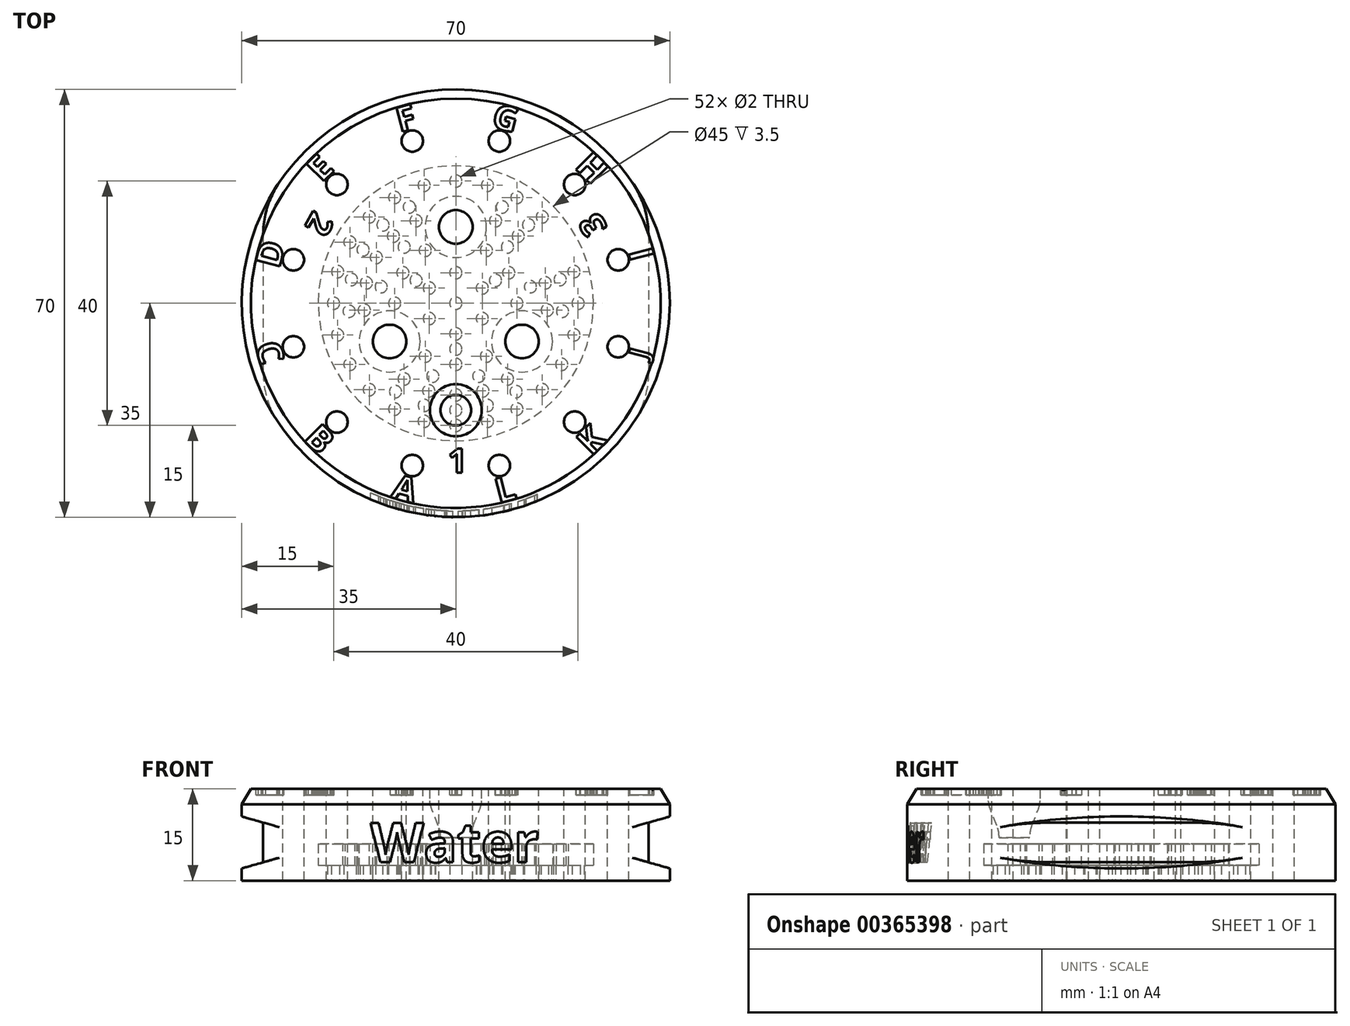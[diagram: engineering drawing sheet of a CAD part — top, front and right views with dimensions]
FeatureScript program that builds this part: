
annotation { "Feature Type Name" : "Feature", "Feature Type Description" : "" }
export const myFeature = defineFeature(function(context is Context, id is Id, definition is map)
    precondition{}
    {
        {
            var Q0;
            Q0=qCreatedBy(makeId("Top.planeOp"),FACE);
            var sketch = newSketch(context, id + "F0", { "sketchPlane" : qUnion([Q0])});
            skCircle(sketch, "E0", {"center": v(0, 0) * mm, "radius": 35 * mm});
            skSolve(sketch);
        }
        {
            var Q0;
            Q0=qSketchRegion(id+"F0",true);
            extrude(context, id + "F1", {"entities" : qUnion([Q0]), "depth" : 15 * mm});
        }
        {
            var Q0;
            Q0=qCreatedBy(makeId("Front.planeOp"),FACE);
            var sketch = newSketch(context, id + "F2", { "sketchPlane" : qUnion([Q0])});
            skText(sketch, "E1", { "text": "Water", "fontName": "OpenSans-Bold.ttf"});
            const initialGuessF2  = {"E1": [-0.01396, 0.003, 1, 0, 0.0065]};
            skSetInitialGuess(sketch, initialGuessF2);
            skSolve(sketch);
        }
        {
            var Q0;
            Q0=qSketchRegion(id+"F2",true);
            var Q1;
            Q1=makeQuery(id+"F1.opExtrude","SWEPT_FACE",FACE,{"disambiguationData":[OSD([sQuery(id+"F0.wireOp",EDGE,"E0")])]});
            extrude(context, id + "F3", {"entities" : qUnion([Q0]), "operationType" : NewBodyOperationType.REMOVE, "endBound" : BoundingType.THROUGH_ALL, "endBoundEntityFace" : qUnion([Q1]), "depth" : 25 * mm});
        }
        {
            var Q0;
            Q0=makeQuery(id+"F1.opExtrude","CAP_FACE",FACE,{"disambiguationData":[OSD([sQuery(id+"F0.wireOp",EDGE,"E0")])],"isStart":false});
            var sketch = newSketch(context, id + "F4", { "sketchPlane" : qUnion([Q0])});
            skCircle(sketch, "E2", {"center": v(0, 0) * mm, "radius": 34 * mm});
            skSolve(sketch);
        }
        {
            var Q0;
            Q0=qSketchRegion(id+"F4",true);
            var Q1;
            Q1=makeQuery(id+"F1.opExtrude","CAP_FACE",FACE,{"disambiguationData":[OSD([sQuery(id+"F0.wireOp",EDGE,"E0")])],"isStart":true});
            extrude(context, id + "F5", {"entities" : qUnion([Q0]), "operationType" : NewBodyOperationType.ADD, "endBound" : BoundingType.UP_TO_SURFACE, "oppositeDirection" : true, "endBoundEntityFace" : qUnion([Q1]), "depth" : 25 * mm});
        }
        {
            var Q0;
            Q0=qCreatedBy(makeId("Front.planeOp"),FACE);
            var sketch = newSketch(context, id + "F6", { "sketchPlane" : qUnion([Q0])});
            skLineSegment(sketch, "E3", {"start": v(-35, 10.5) * mm, "end": v(-35, 2) * mm});
            skLineSegment(sketch, "E4", {"start": v(-35, 2) * mm, "end": v(-31.5, 3) * mm});
            skLineSegment(sketch, "E5", {"start": v(-31.5, 3) * mm, "end": v(-31.5, 9.5) * mm});
            skLineSegment(sketch, "E6", {"start": v(-31.5, 9.5) * mm, "end": v(-35, 10.5) * mm});
            skLineSegment(sketch, "E7.MirrorCS", {"start": v(35, 10.5) * mm, "end": v(35, 2) * mm});
            skLineSegment(sketch, "E8.MirrorCS", {"start": v(31.5, 9.5) * mm, "end": v(35, 10.5) * mm});
            skLineSegment(sketch, "E9.MirrorCS", {"start": v(35, 2) * mm, "end": v(31.5, 3) * mm});
            skLineSegment(sketch, "E10.MirrorCS", {"start": v(31.5, 3) * mm, "end": v(31.5, 9.5) * mm});
            skSolve(sketch);
        }
        {
            var Q0;
            Q0=qSketchRegion(id+"F6",true);
            extrude(context, id + "F7", {"entities" : qUnion([Q0]), "operationType" : NewBodyOperationType.REMOVE, "endBound" : BoundingType.THROUGH_ALL, "oppositeDirection" : true, "depth" : 25 * mm, "hasSecondDirection" : true, "secondDirectionBound" : BoundingType.THROUGH_ALL, "secondDirectionOppositeDirection" : false, "secondDirectionDepth" : 25 * mm});
        }
        {
            var Q0;
            {var subQ0=sQuery(id+"F0.wireOp",EDGE,"E0");Q0=makeQuery(id+"F7.boolean.opBoolean","INTERSECT",EDGE,{"disambiguationData":[OD(0.0)],"derivedFrom":[makeQuery(id+"F3.boolean.opBoolean","SPLIT",FACE,{"disambiguationData":[TD([makeQuery(id+"F1.opExtrude","CAP_FACE",FACE,{"disambiguationData":[OSD([subQ0])],"isStart":true})])],"derivedFrom":makeQuery(id+"F1.opExtrude","SWEPT_FACE",FACE,{"disambiguationData":[OSD([subQ0])]})}),makeQuery(id+"F7.opExtrude","SWEPT_FACE",FACE,{"disambiguationData":[OSD([sQuery(id+"F6.wireOp",EDGE,"E5")])]})]});}
            var Q1;
            {var subQ0=sQuery(id+"F0.wireOp",EDGE,"E0");Q1=makeQuery(id+"F7.boolean.opBoolean","INTERSECT",EDGE,{"disambiguationData":[OD(0.0)],"derivedFrom":[makeQuery(id+"F3.boolean.opBoolean","SPLIT",FACE,{"disambiguationData":[TD([makeQuery(id+"F1.opExtrude","CAP_FACE",FACE,{"disambiguationData":[OSD([subQ0])],"isStart":true})])],"derivedFrom":makeQuery(id+"F1.opExtrude","SWEPT_FACE",FACE,{"disambiguationData":[OSD([subQ0])]})}),makeQuery(id+"F7.opExtrude","SWEPT_FACE",FACE,{"disambiguationData":[OSD([sQuery(id+"F6.wireOp",EDGE,"E10.MirrorCS")])]})]});}
            var Q2;
            {var subQ0=sQuery(id+"F0.wireOp",EDGE,"E0");Q2=makeQuery(id+"F7.boolean.opBoolean","INTERSECT",EDGE,{"disambiguationData":[OD(1.0)],"derivedFrom":[makeQuery(id+"F3.boolean.opBoolean","SPLIT",FACE,{"disambiguationData":[TD([makeQuery(id+"F1.opExtrude","CAP_FACE",FACE,{"disambiguationData":[OSD([subQ0])],"isStart":true})])],"derivedFrom":makeQuery(id+"F1.opExtrude","SWEPT_FACE",FACE,{"disambiguationData":[OSD([subQ0])]})}),makeQuery(id+"F7.opExtrude","SWEPT_FACE",FACE,{"disambiguationData":[OSD([sQuery(id+"F6.wireOp",EDGE,"E10.MirrorCS")])]})]});}
            var Q3;
            {var subQ0=sQuery(id+"F0.wireOp",EDGE,"E0");Q3=makeQuery(id+"F7.boolean.opBoolean","INTERSECT",EDGE,{"disambiguationData":[OD(1.0)],"derivedFrom":[makeQuery(id+"F3.boolean.opBoolean","SPLIT",FACE,{"disambiguationData":[TD([makeQuery(id+"F1.opExtrude","CAP_FACE",FACE,{"disambiguationData":[OSD([subQ0])],"isStart":true})])],"derivedFrom":makeQuery(id+"F1.opExtrude","SWEPT_FACE",FACE,{"disambiguationData":[OSD([subQ0])]})}),makeQuery(id+"F7.opExtrude","SWEPT_FACE",FACE,{"disambiguationData":[OSD([sQuery(id+"F6.wireOp",EDGE,"E5")])]})]});}
            fillet(context, id + "F8", {"entities" : qUnion([Q0, Q1, Q2, Q3]), "radius" : 15 * mm, "tangentPropagation" : true, "allowEdgeOverflow" : false});
        }
        {
            var Q0;
            Q0=makeQuery(id+"F1.opExtrude","CAP_FACE",FACE,{"disambiguationData":[OSD([sQuery(id+"F0.wireOp",EDGE,"E0")])],"isStart":false});
            var sketch = newSketch(context, id + "F9", { "sketchPlane" : qUnion([Q0])});
            skCircle(sketch, "E11", {"center": v(0, 12.5) * mm, "radius": 2.75 * mm});
            skCircle(sketch, "E12.1.0", {"center": v(-10.83, -6.25) * mm, "radius": 2.75 * mm});
            skCircle(sketch, "E12.2.0", {"center": v(10.83, -6.25) * mm, "radius": 2.75 * mm});
            skPoint(sketch, "E12.center", {"position": v(0, 0) * mm});
            skCircle(sketch, "E13", {"center": v(0, 0) * mm, "radius": 12.5 * mm, "construction": true});
            skSolve(sketch);
        }
        {
            var Q0;
            Q0=qSketchRegion(id+"F9",true);
            extrude(context, id + "F10", {"entities" : qUnion([Q0]), "operationType" : NewBodyOperationType.REMOVE, "endBound" : BoundingType.THROUGH_ALL, "oppositeDirection" : true, "depth" : 25 * mm});
        }
        {
            var Q0;
            Q0=makeQuery(id+"F1.opExtrude","CAP_FACE",FACE,{"disambiguationData":[OSD([sQuery(id+"F0.wireOp",EDGE,"E0")])],"isStart":false});
            var sketch = newSketch(context, id + "F11", { "sketchPlane" : qUnion([Q0])});
            skCircle(sketch, "E14", {"center": v(0, -17.5) * mm, "radius": 2.5 * mm});
            skCircle(sketch, "E15", {"center": v(0, 0) * mm, "radius": 17.5 * mm, "construction": true});
            skSolve(sketch);
        }
        {
            var Q0;
            Q0=qSketchRegion(id+"F11",true);
            extrude(context, id + "F12", {"entities" : qUnion([Q0]), "operationType" : NewBodyOperationType.REMOVE, "endBound" : BoundingType.THROUGH_ALL, "oppositeDirection" : true, "depth" : 25 * mm});
        }
        {
            var Q0;
            Q0=makeQuery(id+"F1.opExtrude","CAP_FACE",FACE,{"disambiguationData":[OSD([sQuery(id+"F0.wireOp",EDGE,"E0")])],"isStart":false});
            var sketch = newSketch(context, id + "F13", { "sketchPlane" : qUnion([Q0])});
            skCircle(sketch, "E16", {"center": v(0, -17.5) * mm, "radius": 4.25 * mm});
            skSolve(sketch);
        }
        {
            var Q0;
            Q0=qSketchRegion(id+"F13",true);
            extrude(context, id + "F14", {"entities" : qUnion([Q0]), "operationType" : NewBodyOperationType.REMOVE, "oppositeDirection" : true, "depth" : 7.5 * mm});
        }
        {
            var Q0;
            Q0=makeQuery(id+"F14.boolean.opBoolean","COPY",EDGE,{"derivedFrom":makeQuery(id+"F14.opExtrude","CAP_EDGE",EDGE,{"disambiguationData":[OSD([sQuery(id+"F13.wireOp",EDGE,"E16")])],"isStart":false})});
            chamfer(context, id + "F15", {"entities" : qUnion([Q0]), "chamferType" : ChamferType.TWO_OFFSETS, "width1" : 5 * mm, "oppositeDirection" : true, "width2" : 2 * mm, "tangentPropagation" : true});
        }
        {
            var Q0;
            {var subQ0=sQuery(id+"F13.wireOp",EDGE,"E16");Q0=makeQuery(id+"F15.opChamfer","BLEND_EDGE",EDGE,{"blendedFrom":[makeQuery(id+"F14.boolean.opBoolean","COPY",EDGE,{"derivedFrom":makeQuery(id+"F14.opExtrude","CAP_EDGE",EDGE,{"disambiguationData":[OSD([subQ0])],"isStart":false})}),makeQuery(id+"F14.boolean.opBoolean","COPY",FACE,{"derivedFrom":makeQuery(id+"F14.opExtrude","SWEPT_FACE",FACE,{"disambiguationData":[OSD([subQ0])]})})],"blendedInto":[makeQuery(id+"F14.boolean.opBoolean","COPY",FACE,{"derivedFrom":makeQuery(id+"F14.opExtrude","SWEPT_FACE",FACE,{"disambiguationData":[OSD([subQ0])]})})]});}
            var Q1;
            Q1=makeQuery(id+"F15.opChamfer","BLEND_EDGE",EDGE,{"blendedFrom":[makeQuery(id+"F14.boolean.opBoolean","COPY",EDGE,{"derivedFrom":makeQuery(id+"F14.opExtrude","CAP_EDGE",EDGE,{"disambiguationData":[OSD([sQuery(id+"F13.wireOp",EDGE,"E16")])],"isStart":false})}),makeQuery(id+"F12.boolean.opBoolean","COPY",FACE,{"derivedFrom":makeQuery(id+"F12.opExtrude","SWEPT_FACE",FACE,{"disambiguationData":[OSD([sQuery(id+"F11.wireOp",EDGE,"E14")])]})})],"blendedInto":[makeQuery(id+"F12.boolean.opBoolean","COPY",FACE,{"derivedFrom":makeQuery(id+"F12.opExtrude","SWEPT_FACE",FACE,{"disambiguationData":[OSD([sQuery(id+"F11.wireOp",EDGE,"E14")])]})})]});
            fillet(context, id + "F16", {"entities" : qUnion([Q0, Q1]), "radius" : 5 * mm, "tangentPropagation" : true, "allowEdgeOverflow" : false});
        }
        {
            var Q0;
            Q0=makeQuery(id+"F1.opExtrude","CAP_FACE",FACE,{"disambiguationData":[OSD([sQuery(id+"F0.wireOp",EDGE,"E0")])],"isStart":false});
            var sketch = newSketch(context, id + "F17", { "sketchPlane" : qUnion([Q0])});
            skCircle(sketch, "E17", {"center": v(19.45, 19.45) * mm, "radius": 1.75 * mm});
            skCircle(sketch, "E18", {"center": v(0, 0) * mm, "radius": 27.5 * mm, "construction": true});
            skLineSegment(sketch, "E19", {"start": v(0, 0) * mm, "end": v(19.45, 19.45) * mm, "construction": true});
            skCircle(sketch, "E20.1.1", {"center": v(7.12, 26.56) * mm, "radius": 1.75 * mm});
            skCircle(sketch, "E20.2.1", {"center": v(-7.12, 26.56) * mm, "radius": 1.75 * mm});
            skCircle(sketch, "E20.3.1", {"center": v(-19.45, 19.45) * mm, "radius": 1.75 * mm});
            skCircle(sketch, "E20.4.1", {"center": v(-26.56, 7.12) * mm, "radius": 1.75 * mm});
            skCircle(sketch, "E20.5.1", {"center": v(-26.56, -7.12) * mm, "radius": 1.75 * mm});
            skCircle(sketch, "E20.6.1", {"center": v(-19.45, -19.45) * mm, "radius": 1.75 * mm});
            skCircle(sketch, "E20.7.1", {"center": v(-7.12, -26.56) * mm, "radius": 1.75 * mm});
            skCircle(sketch, "E20.8.1", {"center": v(7.12, -26.56) * mm, "radius": 1.75 * mm});
            skCircle(sketch, "E20.9.1", {"center": v(19.45, -19.45) * mm, "radius": 1.75 * mm});
            skCircle(sketch, "E20.10.1", {"center": v(26.56, -7.12) * mm, "radius": 1.75 * mm});
            skCircle(sketch, "E20.11.1", {"center": v(26.56, 7.12) * mm, "radius": 1.75 * mm});
            skSolve(sketch);
        }
        {
            var Q0;
            Q0=qSketchRegion(id+"F17",true);
            extrude(context, id + "F18", {"entities" : qUnion([Q0]), "operationType" : NewBodyOperationType.REMOVE, "endBound" : BoundingType.THROUGH_ALL, "oppositeDirection" : true, "depth" : 25 * mm});
        }
        {
            var Q0;
            Q0=makeQuery(id+"F1.opExtrude","CAP_EDGE",EDGE,{"disambiguationData":[OSD([sQuery(id+"F0.wireOp",EDGE,"E0")])],"isStart":false});
            chamfer(context, id + "F19", {"entities" : qUnion([Q0]), "chamferType" : ChamferType.TWO_OFFSETS, "width1" : 2.5 * mm, "oppositeDirection" : true, "width2" : 1.5 * mm, "tangentPropagation" : true});
        }
        {
            var Q0;
            Q0=makeQuery(id+"F1.opExtrude","CAP_FACE",FACE,{"disambiguationData":[OSD([sQuery(id+"F0.wireOp",EDGE,"E0")])],"isStart":false});
            var sketch = newSketch(context, id + "F20", { "sketchPlane" : qUnion([Q0])});
            skText(sketch, "E21", { "text": "A", "fontName": "OpenSans-Bold.ttf"});
            skText(sketch, "E22", { "text": "B", "fontName": "OpenSans-Bold.ttf"});
            skText(sketch, "E23", { "text": "C", "fontName": "OpenSans-Bold.ttf"});
            skText(sketch, "E24", { "text": "E", "fontName": "OpenSans-Bold.ttf"});
            skText(sketch, "E25", { "text": "F", "fontName": "OpenSans-Bold.ttf"});
            skText(sketch, "E26", { "text": "G", "fontName": "OpenSans-Bold.ttf"});
            skText(sketch, "E27", { "text": "H", "fontName": "OpenSans-Bold.ttf"});
            skText(sketch, "E28", { "text": "I", "fontName": "OpenSans-Bold.ttf"});
            skText(sketch, "E29", { "text": "J", "fontName": "OpenSans-Bold.ttf"});
            skText(sketch, "E30", { "text": "K", "fontName": "OpenSans-Bold.ttf"});
            skText(sketch, "E31", { "text": "L", "fontName": "OpenSans-Bold.ttf"});
            skText(sketch, "E32", { "text": "D", "fontName": "OpenSans-Bold.ttf"});
            skCircle(sketch, "E33", {"center": v(0, 0) * mm, "radius": 29.38 * mm, "construction": true});
            skText(sketch, "E34", { "text": "1", "fontName": "OpenSans-Bold.ttf"});
            skText(sketch, "E35", { "text": "2", "fontName": "OpenSans-Bold.ttf"});
            skText(sketch, "E36", { "text": "3", "fontName": "OpenSans-Bold.ttf"});
            skCircle(sketch, "E37", {"center": v(0, 0) * mm, "radius": 23.75 * mm, "construction": true});
            const initialGuessF20  = {"E21": [-0.0107, -0.03174, 0.96593, -0.25882, 0.00406], "E22": [-0.025, -0.02228, 0.7071, -0.7071, 0.00406], "E23": [-0.03278, -0.00684, 0.25882, -0.96593, 0.00406], "E24": [-0.0219, 0.01964, 0.7071, 0.7071, 0.00406], "E25": [-0.00914, 0.02796, 0.96593, 0.25882, 0.00406], "E26": [0.00567, 0.0289, 0.96593, -0.25882, 0.00406], "E27": [0.0193, 0.02225, 0.7071, -0.7071, 0.00406], "E28": [0.02815, 0.00844, 0.25882, -0.96593, 0.00406], "E29": [0.0313, -0.00927, 0.25882, 0.96593, 0.00325], "E30": [0.02219, -0.0251, 0.7071, 0.7071, 0.00406], "E31": [0.00703, -0.03273, 0.96593, 0.25882, 0.00406], "E32": [-0.02892, 0.00557, 0.25882, 0.96593, 0.00406], "E34": [-0.00133, -0.02775, 1, 0, 0.004], "E35": [-0.0232, 0.01533, -0.5, -0.86603, 0.004], "E36": [0.02486, 0.01244, -0.5, 0.86603, 0.004]};
            skSetInitialGuess(sketch, initialGuessF20);
            skSolve(sketch);
        }
        {
            var Q0;
            Q0=qSketchRegion(id+"F20",true);
            extrude(context, id + "F21", {"entities" : qUnion([Q0]), "operationType" : NewBodyOperationType.REMOVE, "oppositeDirection" : true, "depth" : 1 * mm});
        }
        {
            var Q0;
            Q0=makeQuery(id+"F1.opExtrude","CAP_FACE",FACE,{"disambiguationData":[OSD([sQuery(id+"F0.wireOp",EDGE,"E0")])],"isStart":true});
            var sketch = newSketch(context, id + "F22", { "sketchPlane" : qUnion([Q0])});
            skCircle(sketch, "E38.0", {"center": v(0, 17.5) * mm, "radius": 2.5 * mm});
            skCircle(sketch, "E38.1", {"center": v(-15.16, -8.75) * mm, "radius": 2.5 * mm});
            skSolve(sketch);
        }
        {
            var Q0;
            Q0=qSketchRegion(id+"F22",true);
            extrude(context, id + "F23", {"entities" : qUnion([Q0]), "operationType" : NewBodyOperationType.ADD, "oppositeDirection" : true, "depth" : 7 * mm});
        }
        {
            var Q0;
            Q0=makeQuery(id+"F23.boolean.opBoolean","MERGE",FACE,{"derivedFrom":[makeQuery(id+"F1.opExtrude","CAP_FACE",FACE,{"disambiguationData":[OSD([sQuery(id+"F0.wireOp",EDGE,"E0")])],"isStart":true}),makeQuery(id+"F23.opExtrude","CAP_FACE",FACE,{"disambiguationData":[OSD([sQuery(id+"F22.wireOp",EDGE,"E38.0")])],"isStart":true}),makeQuery(id+"F23.opExtrude","CAP_FACE",FACE,{"disambiguationData":[OSD([sQuery(id+"F22.wireOp",EDGE,"E38.1")])],"isStart":true})]});
            var sketch = newSketch(context, id + "F24", { "sketchPlane" : qUnion([Q0])});
            skCircle(sketch, "E39", {"center": v(0, 0) * mm, "radius": 22.5 * mm});
            skCircle(sketch, "E40", {"center": v(10.83, 6.25) * mm, "radius": 5 * mm});
            skCircle(sketch, "E41", {"center": v(-10.83, 6.25) * mm, "radius": 5 * mm});
            skCircle(sketch, "E42", {"center": v(0, -12.5) * mm, "radius": 5 * mm});
            skSolve(sketch);
        }
        {
            var Q0;
            Q0=qSketchRegion(id+"F24",true);
            extrude(context, id + "F25", {"entities" : qUnion([Q0]), "operationType" : NewBodyOperationType.REMOVE, "oppositeDirection" : true, "depth" : 6 * mm});
        }
        {
            var Q0;
            Q0=makeQuery(id+"F25.boolean.opBoolean","COPY",FACE,{"derivedFrom":makeQuery(id+"F25.opExtrude","CAP_FACE",FACE,{"disambiguationData":[OSD([sQuery(id+"F24.wireOp",EDGE,"E39"),sQuery(id+"F24.wireOp",EDGE,"E40"),sQuery(id+"F24.wireOp",EDGE,"E41"),sQuery(id+"F24.wireOp",EDGE,"E42")])],"isStart":false})});
            var sketch = newSketch(context, id + "F26", { "sketchPlane" : qUnion([Q0])});
            skCircle(sketch, "E43", {"center": v(0, 0) * mm, "radius": 1 * mm});
            skCircle(sketch, "E44", {"center": v(0, 7.5) * mm, "radius": 1 * mm});
            skCircle(sketch, "E45", {"center": v(3.76, 11.92) * mm, "radius": 1 * mm});
            skCircle(sketch, "E46", {"center": v(-3.76, 11.92) * mm, "radius": 1 * mm});
            skCircle(sketch, "E47", {"center": v(0, 17.5) * mm, "radius": 1 * mm});
            skLineSegment(sketch, "E48", {"start": v(3.76, 11.92) * mm, "end": v(0, 0) * mm, "construction": true});
            skCircle(sketch, "E49.1.0", {"center": v(-6.5, -3.75) * mm, "radius": 1 * mm});
            skCircle(sketch, "E49.1.1", {"center": v(-8.44, -9.22) * mm, "radius": 1 * mm});
            skCircle(sketch, "E49.1.2", {"center": v(-12.2, -2.7) * mm, "radius": 1 * mm});
            skCircle(sketch, "E49.2.0", {"center": v(6.5, -3.75) * mm, "radius": 1 * mm});
            skCircle(sketch, "E49.2.1", {"center": v(12.2, -2.7) * mm, "radius": 1 * mm});
            skCircle(sketch, "E49.2.2", {"center": v(8.44, -9.22) * mm, "radius": 1 * mm});
            skCircle(sketch, "E50.1.0", {"center": v(-5.16, 16.72) * mm, "radius": 1 * mm});
            skCircle(sketch, "E50.2.0", {"center": v(-9.86, 14.46) * mm, "radius": 1 * mm});
            skCircle(sketch, "E50.5.0", {"center": v(-17.45, 1.3) * mm, "radius": 1 * mm});
            skCircle(sketch, "E50.6.0", {"center": v(-17.06, -3.9) * mm, "radius": 1 * mm});
            skCircle(sketch, "E50.7.0", {"center": v(-15.16, -8.75) * mm, "radius": 1 * mm});
            skCircle(sketch, "E50.8.0", {"center": v(-11.9, -12.83) * mm, "radius": 1 * mm});
            skCircle(sketch, "E50.9.0", {"center": v(-7.6, -15.77) * mm, "radius": 1 * mm});
            skCircle(sketch, "E50.12.0", {"center": v(7.6, -15.77) * mm, "radius": 1 * mm});
            skCircle(sketch, "E50.13.0", {"center": v(11.9, -12.83) * mm, "radius": 1 * mm});
            skCircle(sketch, "E50.15.0", {"center": v(17.06, -3.9) * mm, "radius": 1 * mm});
            skCircle(sketch, "E50.16.0", {"center": v(17.45, 1.3) * mm, "radius": 1 * mm});
            skCircle(sketch, "E50.19.0", {"center": v(9.86, 14.46) * mm, "radius": 1 * mm});
            skCircle(sketch, "E50.20.0", {"center": v(5.16, 16.72) * mm, "radius": 1 * mm});
            skSolve(sketch);
        }
        {
            var Q0;
            Q0=qSketchRegion(id+"F26",true);
            var Q1;
            {var subQ0=sQuery(id+"F0.wireOp",EDGE,"E0");Q1=makeQuery(id+"F25.boolean.opBoolean","SPLIT",FACE,{"disambiguationData":[TD([makeQuery(id+"F1.opExtrude","SWEPT_FACE",FACE,{"disambiguationData":[OSD([subQ0])]})])],"derivedFrom":makeQuery(id+"F23.boolean.opBoolean","MERGE",FACE,{"derivedFrom":[makeQuery(id+"F1.opExtrude","CAP_FACE",FACE,{"disambiguationData":[OSD([subQ0])],"isStart":true}),makeQuery(id+"F23.opExtrude","CAP_FACE",FACE,{"disambiguationData":[OSD([sQuery(id+"F22.wireOp",EDGE,"E38.0")])],"isStart":true}),makeQuery(id+"F23.opExtrude","CAP_FACE",FACE,{"disambiguationData":[OSD([sQuery(id+"F22.wireOp",EDGE,"E38.1")])],"isStart":true})]})});}
            extrude(context, id + "F27", {"entities" : qUnion([Q0]), "operationType" : NewBodyOperationType.ADD, "endBound" : BoundingType.UP_TO_SURFACE, "endBoundEntityFace" : qUnion([Q1]), "depth" : 25 * mm});
        }
        {
            var Q0;
            {var subQ0=sQuery(id+"F0.wireOp",EDGE,"E0");Q0=makeQuery(id+"F25.boolean.opBoolean","SPLIT",FACE,{"disambiguationData":[TD([makeQuery(id+"F1.opExtrude","SWEPT_FACE",FACE,{"disambiguationData":[OSD([subQ0])]})])],"derivedFrom":makeQuery(id+"F23.boolean.opBoolean","MERGE",FACE,{"derivedFrom":[makeQuery(id+"F1.opExtrude","CAP_FACE",FACE,{"disambiguationData":[OSD([subQ0])],"isStart":true}),makeQuery(id+"F23.opExtrude","CAP_FACE",FACE,{"disambiguationData":[OSD([sQuery(id+"F22.wireOp",EDGE,"E38.0")])],"isStart":true}),makeQuery(id+"F23.opExtrude","CAP_FACE",FACE,{"disambiguationData":[OSD([sQuery(id+"F22.wireOp",EDGE,"E38.1")])],"isStart":true})]})});}
            var sketch = newSketch(context, id + "F28", { "sketchPlane" : qUnion([Q0])});
            skCircle(sketch, "E51.0", {"center": v(0, 0) * mm, "radius": 22.5 * mm});
            skCircle(sketch, "E52.0", {"center": v(-10.83, 6.25) * mm, "radius": 2.75 * mm});
            skCircle(sketch, "E52.1", {"center": v(10.83, 6.25) * mm, "radius": 2.75 * mm});
            skCircle(sketch, "E52.2", {"center": v(0, -12.5) * mm, "radius": 2.75 * mm});
            skSolve(sketch);
        }
        {
            var Q0;
            Q0=qSketchRegion(id+"F28",true);
            extrude(context, id + "F29", {"entities" : qUnion([Q0]), "operationType" : NewBodyOperationType.ADD, "oppositeDirection" : true, "depth" : 2.5 * mm});
        }
        {
            var Q0;
            {var subQ0=sQuery(id+"F0.wireOp",EDGE,"E0");var subQ1=makeQuery(id+"F23.boolean.opBoolean","MERGE",FACE,{"derivedFrom":[makeQuery(id+"F1.opExtrude","CAP_FACE",FACE,{"disambiguationData":[OSD([subQ0])],"isStart":true}),makeQuery(id+"F23.opExtrude","CAP_FACE",FACE,{"disambiguationData":[OSD([sQuery(id+"F22.wireOp",EDGE,"E38.0")])],"isStart":true}),makeQuery(id+"F23.opExtrude","CAP_FACE",FACE,{"disambiguationData":[OSD([sQuery(id+"F22.wireOp",EDGE,"E38.1")])],"isStart":true})]});Q0=makeQuery(id+"F29.boolean.opBoolean","MERGE",FACE,{"derivedFrom":[makeQuery(id+"F25.boolean.opBoolean","SPLIT",FACE,{"disambiguationData":[TD([makeQuery(id+"F1.opExtrude","SWEPT_FACE",FACE,{"disambiguationData":[OSD([subQ0])]})])],"derivedFrom":subQ1}),makeQuery(id+"F25.boolean.opBoolean","SPLIT",FACE,{"disambiguationData":[TD([makeQuery(id+"F10.boolean.opBoolean","COPY",FACE,{"derivedFrom":makeQuery(id+"F10.opExtrude","SWEPT_FACE",FACE,{"disambiguationData":[OSD([sQuery(id+"F9.wireOp",EDGE,"E11")])]})})])],"derivedFrom":subQ1}),makeQuery(id+"F25.boolean.opBoolean","SPLIT",FACE,{"disambiguationData":[TD([makeQuery(id+"F10.boolean.opBoolean","COPY",FACE,{"derivedFrom":makeQuery(id+"F10.opExtrude","SWEPT_FACE",FACE,{"disambiguationData":[OSD([sQuery(id+"F9.wireOp",EDGE,"E12.1.0")])]})})])],"derivedFrom":subQ1}),makeQuery(id+"F25.boolean.opBoolean","SPLIT",FACE,{"disambiguationData":[TD([makeQuery(id+"F10.boolean.opBoolean","COPY",FACE,{"derivedFrom":makeQuery(id+"F10.opExtrude","SWEPT_FACE",FACE,{"disambiguationData":[OSD([sQuery(id+"F9.wireOp",EDGE,"E12.2.0")])]})})])],"derivedFrom":subQ1}),makeQuery(id+"F27.opExtrude","CAP_FACE",FACE,{"disambiguationData":[OSD([sQuery(id+"F26.wireOp",EDGE,"E43")])],"isStart":false}),makeQuery(id+"F27.opExtrude","CAP_FACE",FACE,{"disambiguationData":[OSD([sQuery(id+"F26.wireOp",EDGE,"E44")])],"isStart":false}),makeQuery(id+"F27.opExtrude","CAP_FACE",FACE,{"disambiguationData":[OSD([sQuery(id+"F26.wireOp",EDGE,"E45")])],"isStart":false}),makeQuery(id+"F27.opExtrude","CAP_FACE",FACE,{"disambiguationData":[OSD([sQuery(id+"F26.wireOp",EDGE,"E46")])],"isStart":false}),makeQuery(id+"F27.opExtrude","CAP_FACE",FACE,{"disambiguationData":[OSD([sQuery(id+"F26.wireOp",EDGE,"E47")])],"isStart":false}),makeQuery(id+"F27.opExtrude","CAP_FACE",FACE,{"disambiguationData":[OSD([sQuery(id+"F26.wireOp",EDGE,"E49.1.0")])],"isStart":false}),makeQuery(id+"F27.opExtrude","CAP_FACE",FACE,{"disambiguationData":[OSD([sQuery(id+"F26.wireOp",EDGE,"E49.1.1")])],"isStart":false}),makeQuery(id+"F27.opExtrude","CAP_FACE",FACE,{"disambiguationData":[OSD([sQuery(id+"F26.wireOp",EDGE,"E49.1.2")])],"isStart":false}),makeQuery(id+"F27.opExtrude","CAP_FACE",FACE,{"disambiguationData":[OSD([sQuery(id+"F26.wireOp",EDGE,"E49.2.0")])],"isStart":false}),makeQuery(id+"F27.opExtrude","CAP_FACE",FACE,{"disambiguationData":[OSD([sQuery(id+"F26.wireOp",EDGE,"E49.2.1")])],"isStart":false}),makeQuery(id+"F27.opExtrude","CAP_FACE",FACE,{"disambiguationData":[OSD([sQuery(id+"F26.wireOp",EDGE,"E49.2.2")])],"isStart":false}),makeQuery(id+"F27.opExtrude","CAP_FACE",FACE,{"disambiguationData":[OSD([sQuery(id+"F26.wireOp",EDGE,"E50.1.0")])],"isStart":false}),makeQuery(id+"F27.opExtrude","CAP_FACE",FACE,{"disambiguationData":[OSD([sQuery(id+"F26.wireOp",EDGE,"E50.2.0")])],"isStart":false}),makeQuery(id+"F27.opExtrude","CAP_FACE",FACE,{"disambiguationData":[OSD([sQuery(id+"F26.wireOp",EDGE,"E50.5.0")])],"isStart":false}),makeQuery(id+"F27.opExtrude","CAP_FACE",FACE,{"disambiguationData":[OSD([sQuery(id+"F26.wireOp",EDGE,"E50.6.0")])],"isStart":false}),makeQuery(id+"F27.opExtrude","CAP_FACE",FACE,{"disambiguationData":[OSD([sQuery(id+"F26.wireOp",EDGE,"E50.7.0")])],"isStart":false}),makeQuery(id+"F27.opExtrude","CAP_FACE",FACE,{"disambiguationData":[OSD([sQuery(id+"F26.wireOp",EDGE,"E50.8.0")])],"isStart":false}),makeQuery(id+"F27.opExtrude","CAP_FACE",FACE,{"disambiguationData":[OSD([sQuery(id+"F26.wireOp",EDGE,"E50.9.0")])],"isStart":false}),makeQuery(id+"F27.opExtrude","CAP_FACE",FACE,{"disambiguationData":[OSD([sQuery(id+"F26.wireOp",EDGE,"E50.12.0")])],"isStart":false}),makeQuery(id+"F27.opExtrude","CAP_FACE",FACE,{"disambiguationData":[OSD([sQuery(id+"F26.wireOp",EDGE,"E50.13.0")])],"isStart":false}),makeQuery(id+"F27.opExtrude","CAP_FACE",FACE,{"disambiguationData":[OSD([sQuery(id+"F26.wireOp",EDGE,"E50.15.0")])],"isStart":false}),makeQuery(id+"F27.opExtrude","CAP_FACE",FACE,{"disambiguationData":[OSD([sQuery(id+"F26.wireOp",EDGE,"E50.16.0")])],"isStart":false}),makeQuery(id+"F27.opExtrude","CAP_FACE",FACE,{"disambiguationData":[OSD([sQuery(id+"F26.wireOp",EDGE,"E50.19.0")])],"isStart":false}),makeQuery(id+"F27.opExtrude","CAP_FACE",FACE,{"disambiguationData":[OSD([sQuery(id+"F26.wireOp",EDGE,"E50.20.0")])],"isStart":false}),makeQuery(id+"F29.opExtrude","CAP_FACE",FACE,{"disambiguationData":[OSD([sQuery(id+"F28.wireOp",EDGE,"E51.0")])],"isStart":true})]});}
            var sketch = newSketch(context, id + "F30", { "sketchPlane" : qUnion([Q0])});
            skCircle(sketch, "E53", {"center": v(0, 5) * mm, "radius": 1 * mm});
            skCircle(sketch, "E54.0.1.0", {"center": v(0, 10) * mm, "radius": 1 * mm});
            skCircle(sketch, "E54.0.2.0", {"center": v(0, 15) * mm, "radius": 1 * mm});
            skCircle(sketch, "E54.0.3.0", {"center": v(0, 20) * mm, "radius": 1 * mm});
            skLineSegment(sketch, "E54.direction1", {"start": v(0, 5) * mm, "end": v(25, 5) * mm, "construction": true});
            skLineSegment(sketch, "E54.direction2", {"start": v(0, 5) * mm, "end": v(0, 10) * mm, "construction": true});
            skCircle(sketch, "E55.1.0", {"center": v(-4.33, 2.5) * mm, "radius": 1 * mm});
            skCircle(sketch, "E55.2.0", {"center": v(-4.33, -2.5) * mm, "radius": 1 * mm});
            skCircle(sketch, "E55.3.0", {"center": v(0, -5) * mm, "radius": 1 * mm});
            skCircle(sketch, "E55.4.0", {"center": v(4.33, -2.5) * mm, "radius": 1 * mm});
            skCircle(sketch, "E55.5.0", {"center": v(4.33, 2.5) * mm, "radius": 1 * mm});
            skPoint(sketch, "E55.center", {"position": v(0, 0) * mm});
            skCircle(sketch, "E56.1.0", {"center": v(-5, 8.66) * mm, "radius": 1 * mm});
            skCircle(sketch, "E56.3.0", {"center": v(-10, 0) * mm, "radius": 1 * mm});
            skCircle(sketch, "E56.4.0", {"center": v(-8.66, -5) * mm, "radius": 1 * mm});
            skCircle(sketch, "E56.5.0", {"center": v(-5, -8.66) * mm, "radius": 1 * mm});
            skCircle(sketch, "E56.7.0", {"center": v(5, -8.66) * mm, "radius": 1 * mm});
            skCircle(sketch, "E56.8.0", {"center": v(8.66, -5) * mm, "radius": 1 * mm});
            skCircle(sketch, "E56.9.0", {"center": v(10, 0) * mm, "radius": 1 * mm});
            skCircle(sketch, "E56.11.0", {"center": v(5, 8.66) * mm, "radius": 1 * mm});
            skCircle(sketch, "E57.1.0", {"center": v(-4.42, 14.33) * mm, "radius": 1 * mm});
            skCircle(sketch, "E57.2.0", {"center": v(-8.45, 12.4) * mm, "radius": 1 * mm});
            skCircle(sketch, "E57.5.0", {"center": v(-14.96, 1.12) * mm, "radius": 1 * mm});
            skCircle(sketch, "E57.6.0", {"center": v(-14.62, -3.34) * mm, "radius": 1 * mm});
            skCircle(sketch, "E57.7.0", {"center": v(-13, -7.5) * mm, "radius": 1 * mm});
            skCircle(sketch, "E57.8.0", {"center": v(-10.2, -11) * mm, "radius": 1 * mm});
            skCircle(sketch, "E57.9.0", {"center": v(-6.5, -13.51) * mm, "radius": 1 * mm});
            skCircle(sketch, "E57.12.0", {"center": v(6.5, -13.51) * mm, "radius": 1 * mm});
            skCircle(sketch, "E57.13.0", {"center": v(10.2, -11) * mm, "radius": 1 * mm});
            skCircle(sketch, "E57.15.0", {"center": v(14.62, -3.34) * mm, "radius": 1 * mm});
            skCircle(sketch, "E57.16.0", {"center": v(14.96, 1.12) * mm, "radius": 1 * mm});
            skCircle(sketch, "E57.19.0", {"center": v(8.45, 12.4) * mm, "radius": 1 * mm});
            skCircle(sketch, "E57.20.0", {"center": v(4.42, 14.33) * mm, "radius": 1 * mm});
            skCircle(sketch, "E58.1.0", {"center": v(-5.18, 19.32) * mm, "radius": 1 * mm});
            skCircle(sketch, "E58.2.0", {"center": v(-10, 17.32) * mm, "radius": 1 * mm});
            skCircle(sketch, "E58.3.0", {"center": v(-14.14, 14.14) * mm, "radius": 1 * mm});
            skCircle(sketch, "E58.4.0", {"center": v(-17.32, 10) * mm, "radius": 1 * mm});
            skCircle(sketch, "E58.5.0", {"center": v(-19.32, 5.18) * mm, "radius": 1 * mm});
            skCircle(sketch, "E58.6.0", {"center": v(-20, 0) * mm, "radius": 1 * mm});
            skCircle(sketch, "E58.7.0", {"center": v(-19.32, -5.18) * mm, "radius": 1 * mm});
            skCircle(sketch, "E58.8.0", {"center": v(-17.32, -10) * mm, "radius": 1 * mm});
            skCircle(sketch, "E58.9.0", {"center": v(-14.14, -14.14) * mm, "radius": 1 * mm});
            skCircle(sketch, "E58.10.0", {"center": v(-10, -17.32) * mm, "radius": 1 * mm});
            skCircle(sketch, "E58.11.0", {"center": v(-5.18, -19.32) * mm, "radius": 1 * mm});
            skCircle(sketch, "E58.12.0", {"center": v(0, -20) * mm, "radius": 1 * mm});
            skCircle(sketch, "E58.13.0", {"center": v(5.18, -19.32) * mm, "radius": 1 * mm});
            skCircle(sketch, "E58.14.0", {"center": v(10, -17.32) * mm, "radius": 1 * mm});
            skCircle(sketch, "E58.15.0", {"center": v(14.14, -14.14) * mm, "radius": 1 * mm});
            skCircle(sketch, "E58.17.0", {"center": v(19.32, -5.18) * mm, "radius": 1 * mm});
            skCircle(sketch, "E58.18.0", {"center": v(20, 0) * mm, "radius": 1 * mm});
            skCircle(sketch, "E58.19.0", {"center": v(19.32, 5.18) * mm, "radius": 1 * mm});
            skCircle(sketch, "E58.20.0", {"center": v(17.32, 10) * mm, "radius": 1 * mm});
            skCircle(sketch, "E58.21.0", {"center": v(14.14, 14.14) * mm, "radius": 1 * mm});
            skCircle(sketch, "E58.22.0", {"center": v(10, 17.32) * mm, "radius": 1 * mm});
            skCircle(sketch, "E58.23.0", {"center": v(5.18, 19.32) * mm, "radius": 1 * mm});
            skSolve(sketch);
        }
        {
            var Q0;
            Q0=qSketchRegion(id+"F30",true);
            extrude(context, id + "F31", {"entities" : qUnion([Q0]), "operationType" : NewBodyOperationType.REMOVE, "endBound" : BoundingType.UP_TO_NEXT, "oppositeDirection" : true, "depth" : 25 * mm});
        }
    });
